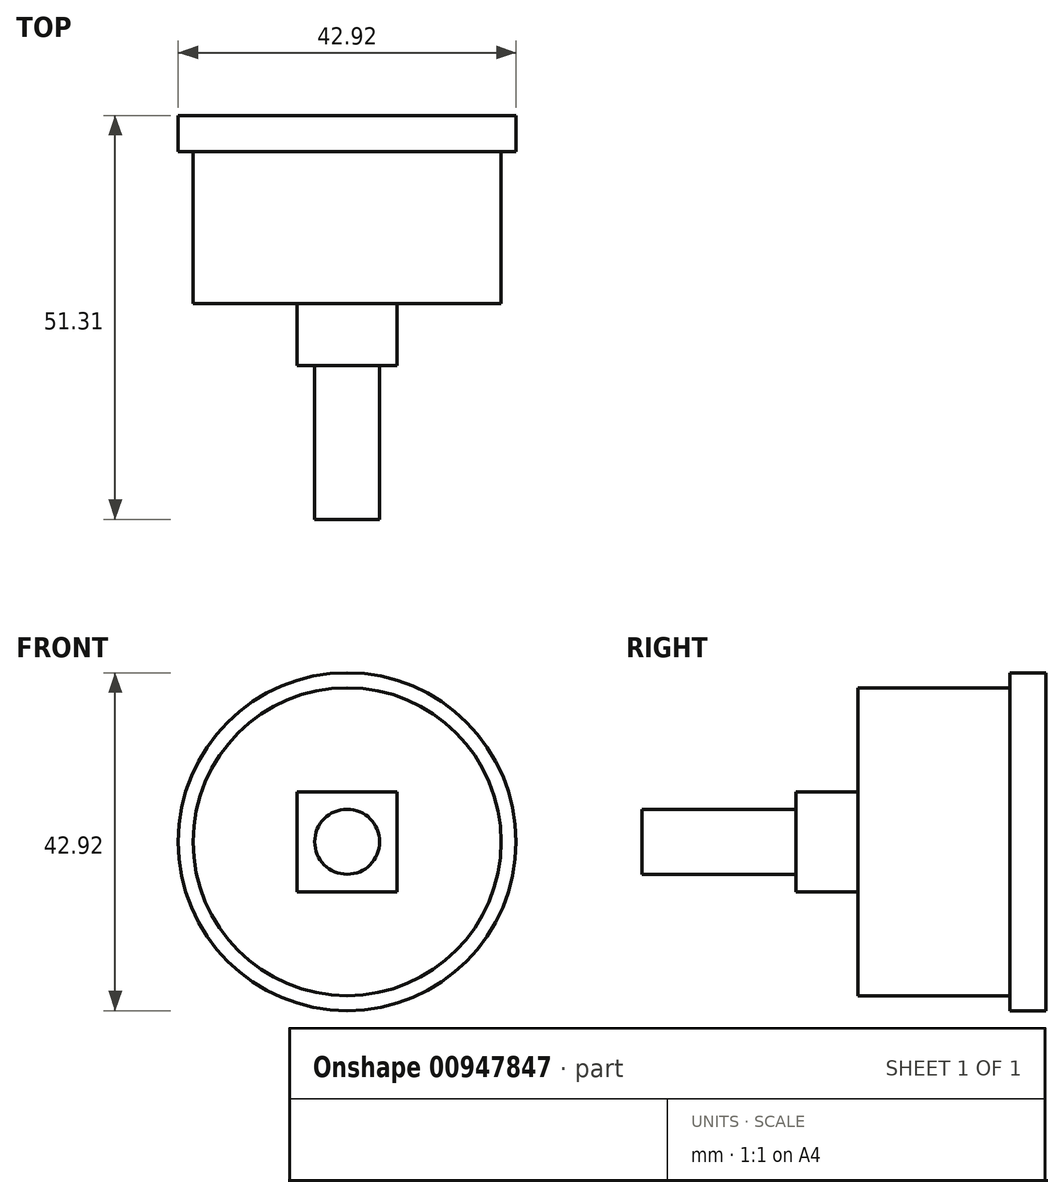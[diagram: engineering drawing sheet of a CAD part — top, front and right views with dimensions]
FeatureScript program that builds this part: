
annotation { "Feature Type Name" : "Feature", "Feature Type Description" : "" }
export const myFeature = defineFeature(function(context is Context, id is Id, definition is map)
    precondition{}
    {
        {
            var Q0;
            Q0=qCreatedBy(makeId("Front.planeOp"),FACE);
            var sketch = newSketch(context, id + "F0", { "sketchPlane" : qUnion([Q0])});
            skCircle(sketch, "E0", {"center": v(0, 0) * mm, "radius": 19.56 * mm});
            skCircle(sketch, "E1", {"center": v(0, 0) * mm, "radius": 21.46 * mm});
            skCircle(sketch, "E2", {"center": v(0, 0) * mm, "radius": 4.13 * mm});
            skLineSegment(sketch, "E3.bottom", {"start": v(-6.35, 6.35) * mm, "end": v(6.35, 6.35) * mm});
            skLineSegment(sketch, "E3.top", {"start": v(-6.35, -6.35) * mm, "end": v(6.35, -6.35) * mm});
            skLineSegment(sketch, "E3.left", {"start": v(-6.35, 6.35) * mm, "end": v(-6.35, -6.35) * mm});
            skLineSegment(sketch, "E3.right", {"start": v(6.35, 6.35) * mm, "end": v(6.35, -6.35) * mm});
            skSolve(sketch);
        }
        {
            var Q0;
            Q0=makeQuery(id+"F0.imprint","IMPRINT",FACE,{"disambiguationData":[TD([[makeQuery(id+"F0.imprint","IMPRINT",EDGE,{"derivedFrom":sQuery(id+"F0.wireOp",EDGE,"E0")}),-1.0]])]});
            extrude(context, id + "F1", {"entities" : qUnion([Q0]), "depth" : 4.57 * mm, "offsetDistance" : 25.4 * mm});
        }
        {
            var Q0;
            Q0=makeQuery(id+"F0.imprint","IMPRINT",FACE,{"disambiguationData":[TD([[makeQuery(id+"F0.imprint","IMPRINT",EDGE,{"derivedFrom":sQuery(id+"F0.wireOp",EDGE,"E0")}),1.0]])]});
            extrude(context, id + "F2", {"entities" : qUnion([Q0]), "operationType" : NewBodyOperationType.ADD, "depth" : 23.88 * mm, "offsetDistance" : 25.4 * mm});
        }
        {
            var Q0;
            Q0=makeQuery(id+"F0.imprint","IMPRINT",FACE,{"disambiguationData":[TD([[makeQuery(id+"F0.imprint","IMPRINT",EDGE,{"derivedFrom":sQuery(id+"F0.wireOp",EDGE,"E2")}),-1.0]])]});
            extrude(context, id + "F3", {"entities" : qUnion([Q0]), "operationType" : NewBodyOperationType.ADD, "depth" : 31.75 * mm, "offsetDistance" : 25.4 * mm});
        }
        {
            var Q0;
            Q0=makeQuery(id+"F0.imprint","IMPRINT",FACE,{"disambiguationData":[TD([[makeQuery(id+"F0.imprint","IMPRINT",EDGE,{"derivedFrom":sQuery(id+"F0.wireOp",EDGE,"E2")}),1.0]])]});
            extrude(context, id + "F4", {"entities" : qUnion([Q0]), "operationType" : NewBodyOperationType.ADD, "depth" : 51.3 * mm, "offsetDistance" : 25.4 * mm});
        }
    });
